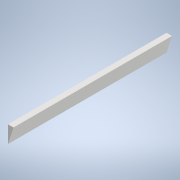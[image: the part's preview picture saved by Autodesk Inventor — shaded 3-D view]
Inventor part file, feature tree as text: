
AUTODESK INVENTOR PART (.ipt)
format: ipt  version: 2020 (Build 240168000, 168)  size: 98,304 bytes
history: native  units: mm
features: other x5, extrude x1, sketch x1
ambient origin geometry x8: Origin, YZ Plane, XZ Plane, XY Plane, X Axis, Y Axis, Z Axis, Center Point
bodies: Body1 (feature_tree)
feature tree (7):
  other  "Sólido1"
  extrude  "Extrusão1"  [1 undecoded]
  sketch  "Esboço1"  dims[d1=144.0mm d2=0.0mm]
  other  "Referência1"
  other  "<userpath>\Desktop\rabo\3d\ela.iam"
  other  "ela.iam"
  other  "guarra_MIR_MIR:1"
note: 1 required parameter value undecoded (feature->parameter linkage not recoverable at this tier; creation-order binding heuristic only, values carry confidence <= 0.55)
